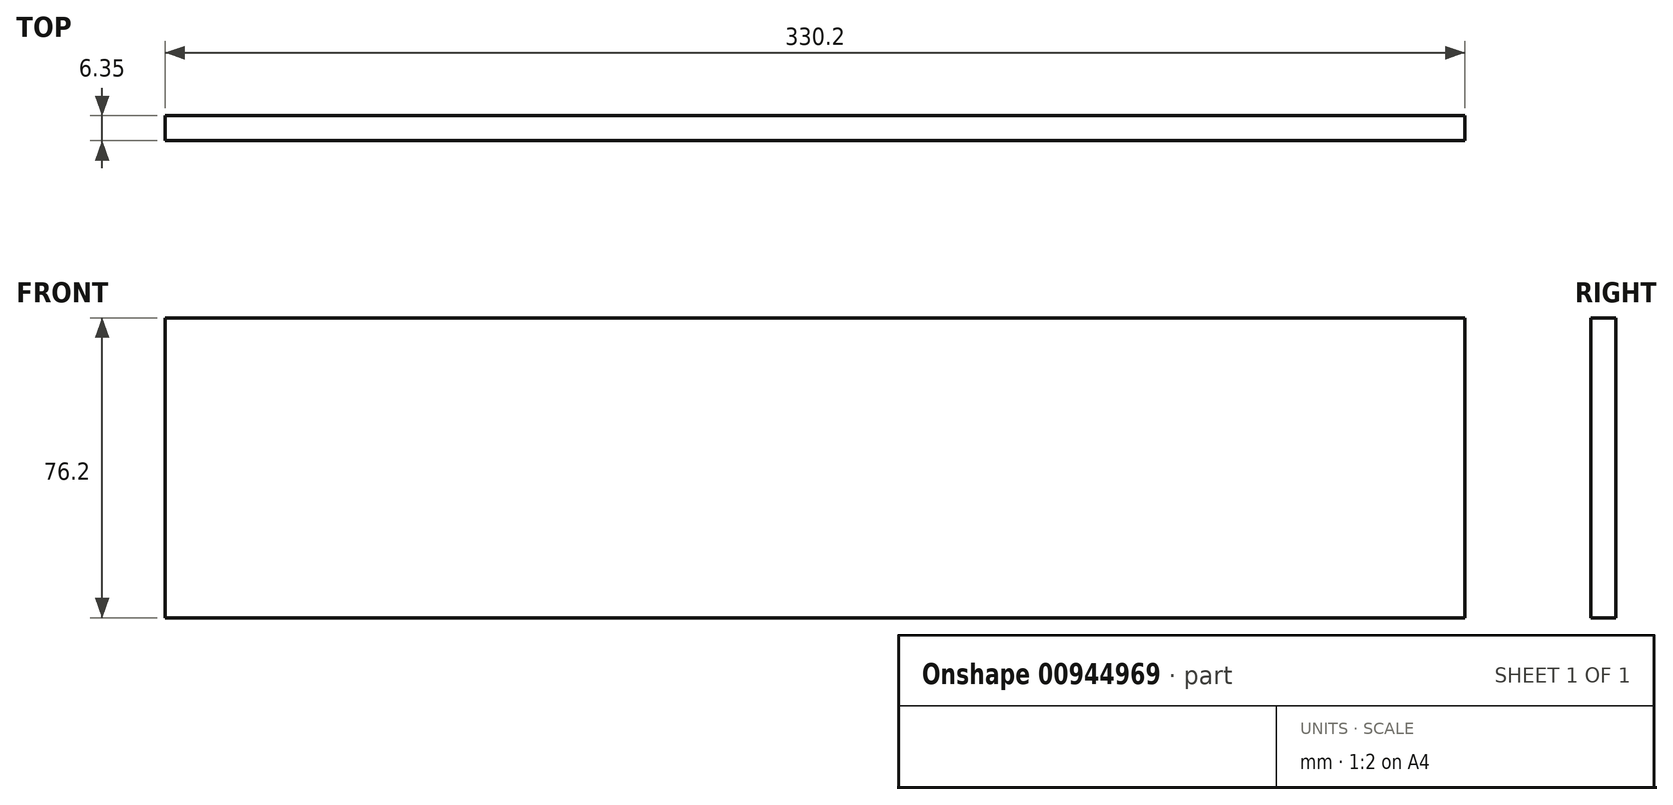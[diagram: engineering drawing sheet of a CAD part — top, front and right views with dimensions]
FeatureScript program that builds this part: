
annotation { "Feature Type Name" : "Feature", "Feature Type Description" : "" }
export const myFeature = defineFeature(function(context is Context, id is Id, definition is map)
    precondition{}
    {
        {
            var Q0;
            Q0=qCreatedBy(makeId("Front.planeOp"),FACE);
            var sketch = newSketch(context, id + "F0", { "sketchPlane" : qUnion([Q0])});
            skLineSegment(sketch, "E0.bottom", {"start": v(0, 0) * mm, "end": v(330.2, 0) * mm});
            skLineSegment(sketch, "E0.top", {"start": v(0, 76.2) * mm, "end": v(330.2, 76.2) * mm});
            skLineSegment(sketch, "E0.left", {"start": v(0, 0) * mm, "end": v(0, 76.2) * mm});
            skLineSegment(sketch, "E0.right", {"start": v(330.2, 0) * mm, "end": v(330.2, 76.2) * mm});
            skSolve(sketch);
        }
        {
            var Q0;
            Q0=makeQuery(id+"F0.imprint","IMPRINT",FACE,{"disambiguationData":[TD([[makeQuery(id+"F0.imprint","IMPRINT",EDGE,{"derivedFrom":sQuery(id+"F0.wireOp",EDGE,"E0.bottom")}),1.0]])]});
            extrude(context, id + "F1", {"entities" : qUnion([Q0]), "oppositeDirection" : true, "depth" : 6.35 * mm, "offsetDistance" : 25.4 * mm});
        }
    });
